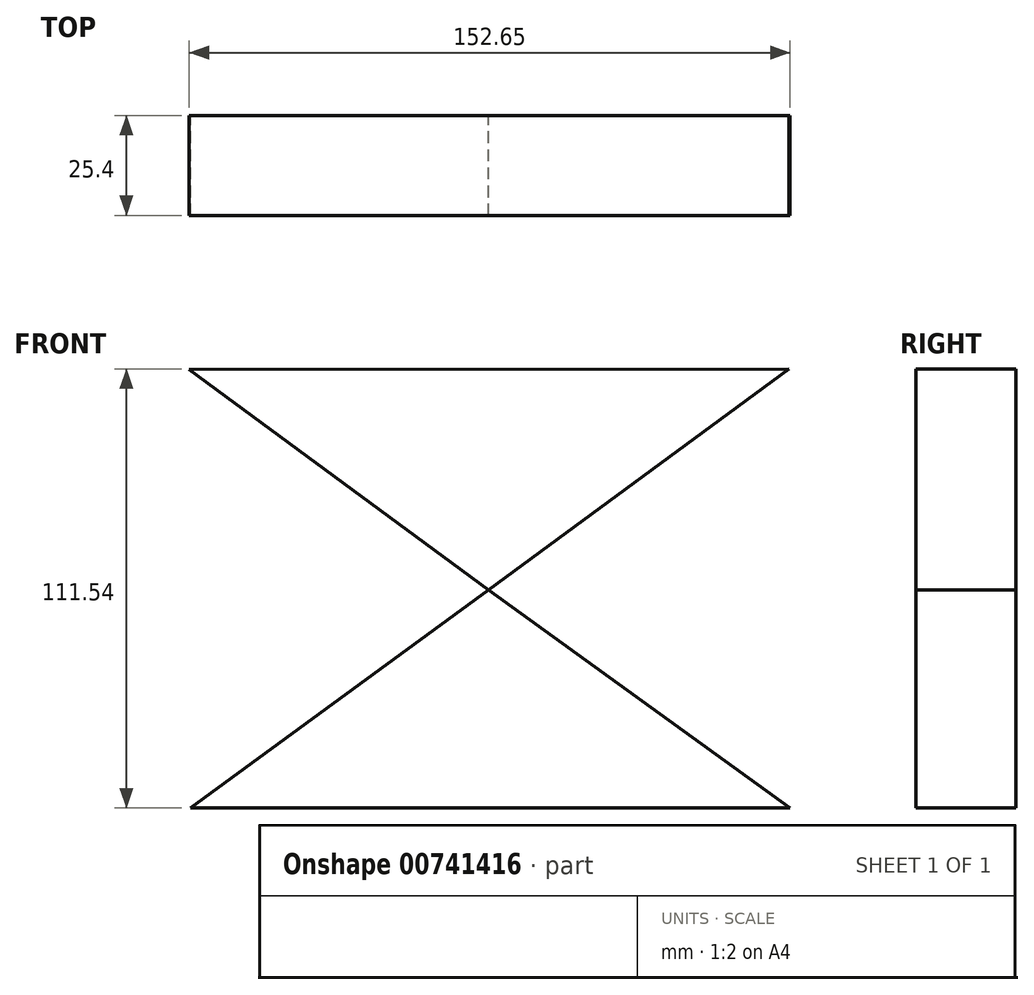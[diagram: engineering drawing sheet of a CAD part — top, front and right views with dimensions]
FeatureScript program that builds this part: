
annotation { "Feature Type Name" : "Feature", "Feature Type Description" : "" }
export const myFeature = defineFeature(function(context is Context, id is Id, definition is map)
    precondition{}
    {
        {
            var Q0;
            Q0=qCreatedBy(makeId("Front.planeOp"),FACE);
            var sketch = newSketch(context, id + "F0", { "sketchPlane" : qUnion([Q0])});
            skLineSegment(sketch, "E0", {"start": v(-76.05, 55.95) * mm, "end": v(0, 0) * mm});
            skLineSegment(sketch, "E1", {"start": v(0, 0) * mm, "end": v(-75.68, -55.4) * mm});
            skLineSegment(sketch, "E2", {"start": v(-75.68, -55.4) * mm, "end": v(76.6, -55.4) * mm});
            skLineSegment(sketch, "E3", {"start": v(76.6, -55.4) * mm, "end": v(0, 0) * mm});
            skLineSegment(sketch, "E4", {"start": v(76.23, 56.14) * mm, "end": v(0, 0) * mm});
            skLineSegment(sketch, "E5", {"start": v(-76.05, 55.95) * mm, "end": v(76.23, 56.14) * mm});
            skSolve(sketch);
        }
        {
            var Q0;
            Q0 = qSketchRegion(id + "F0", true);
            extrude(context, id + "F1", {"entities" : qUnion([Q0]), "depth" : 25.4 * mm, "offsetDistance" : 25.4 * mm});
        }
    });
